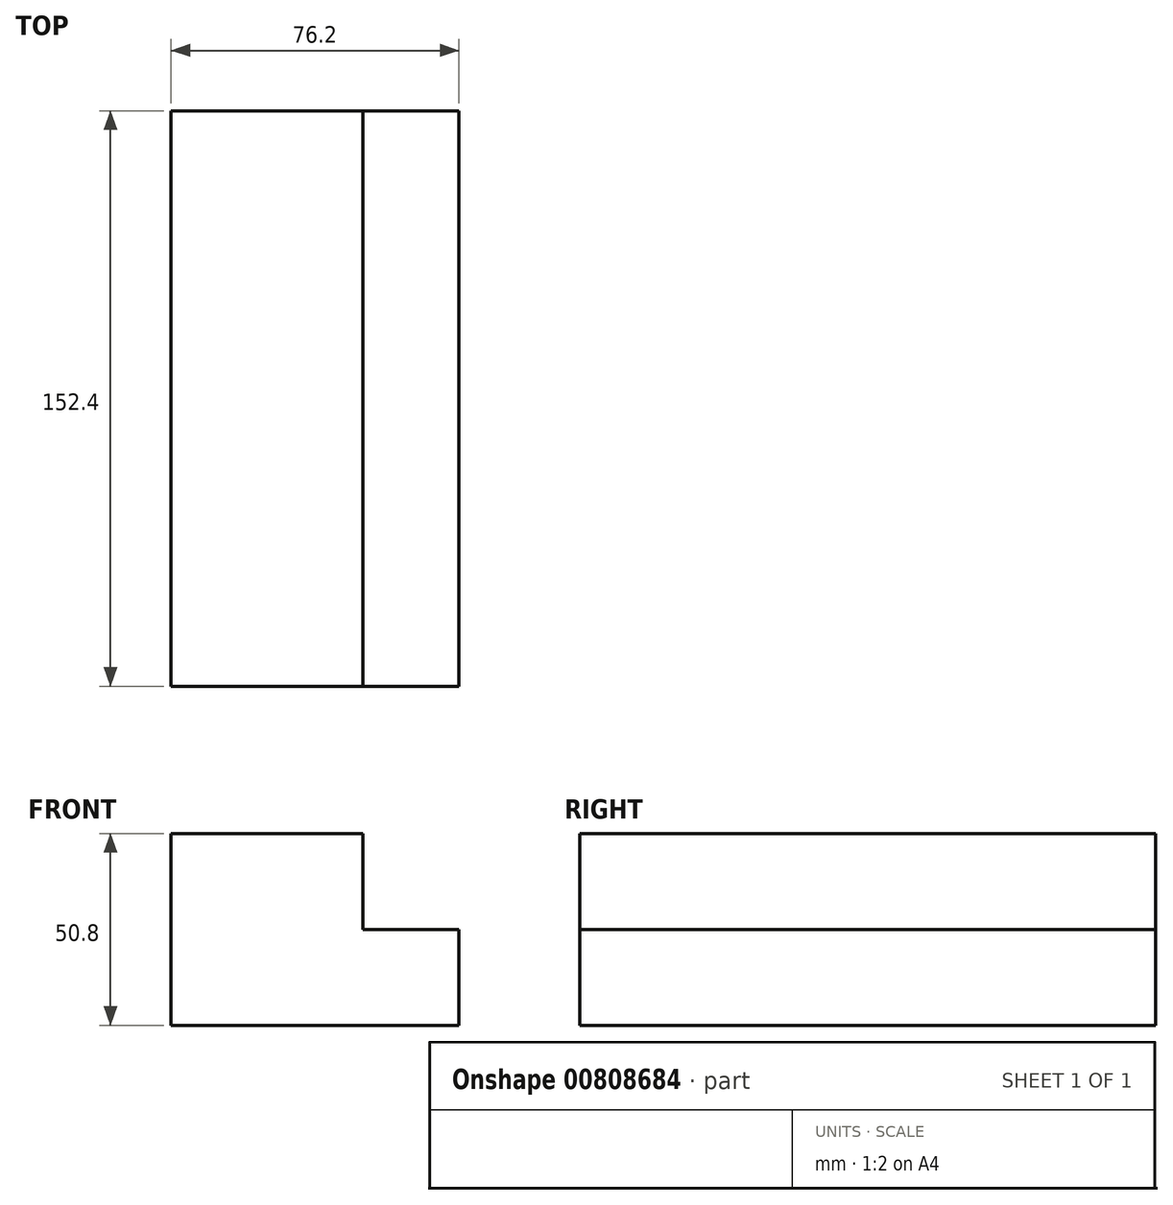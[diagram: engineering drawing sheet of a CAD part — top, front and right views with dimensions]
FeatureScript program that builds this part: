
annotation { "Feature Type Name" : "Feature", "Feature Type Description" : "" }
export const myFeature = defineFeature(function(context is Context, id is Id, definition is map)
    precondition{}
    {
        {
            var Q0;
            Q0=qCreatedBy(makeId("Front.planeOp"),FACE);
            var sketch = newSketch(context, id + "F0", { "sketchPlane" : qUnion([Q0])});
            skLineSegment(sketch, "E0", {"start": v(0, 0) * mm, "end": v(0, 50.8) * mm});
            skLineSegment(sketch, "E1", {"start": v(0, 50.8) * mm, "end": v(50.8, 50.8) * mm});
            skLineSegment(sketch, "E2", {"start": v(50.8, 50.8) * mm, "end": v(50.8, 25.4) * mm});
            skLineSegment(sketch, "E3", {"start": v(50.8, 25.4) * mm, "end": v(76.2, 25.4) * mm});
            skLineSegment(sketch, "E4", {"start": v(76.2, 25.4) * mm, "end": v(76.2, 0) * mm});
            skLineSegment(sketch, "E5", {"start": v(0, 0) * mm, "end": v(76.2, 0) * mm});
            skSolve(sketch);
        }
        {
            var Q0;
            Q0 = qSketchRegion(id + "F0", true);
            extrude(context, id + "F1", {"entities" : qUnion([Q0]), "depth" : 152.4 * mm, "offsetDistance" : 25.4 * mm});
        }
    });
